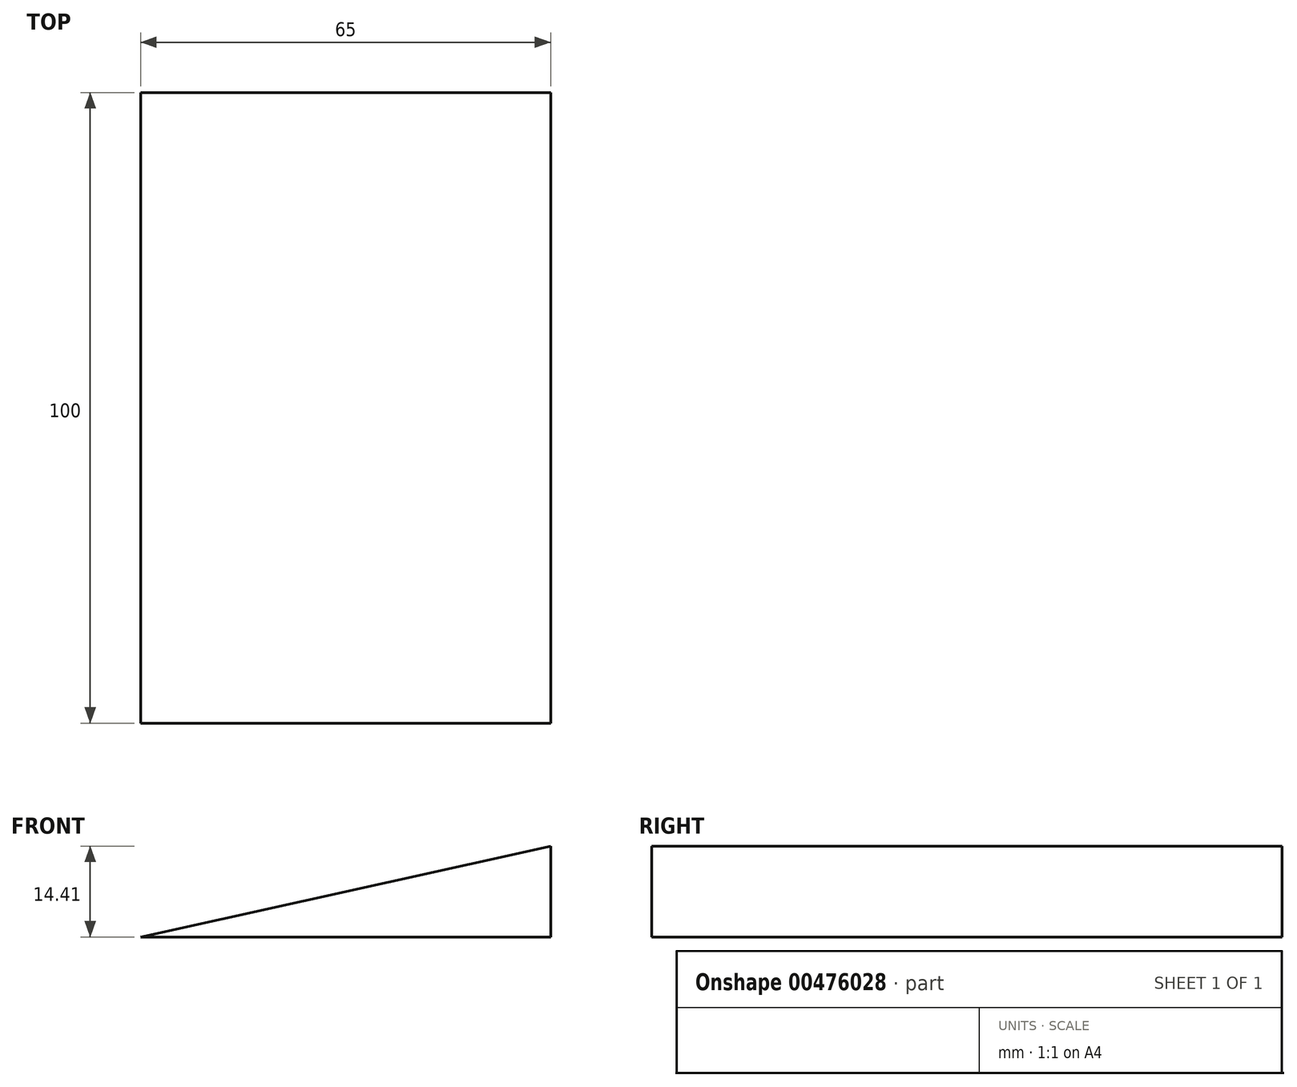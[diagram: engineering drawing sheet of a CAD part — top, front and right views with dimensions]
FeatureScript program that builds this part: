
annotation { "Feature Type Name" : "Feature", "Feature Type Description" : "" }
export const myFeature = defineFeature(function(context is Context, id is Id, definition is map)
    precondition{}
    {
        {
            var Q0;
            Q0=qCreatedBy(makeId("Front.planeOp"),FACE);
            var sketch = newSketch(context, id + "F0", { "sketchPlane" : qUnion([Q0])});
            skLineSegment(sketch, "E0", {"start": v(0, 0) * mm, "end": v(0, 14.41) * mm});
            skLineSegment(sketch, "E1", {"start": v(0, 14.41) * mm, "end": v(-65, 0) * mm});
            skLineSegment(sketch, "E2", {"start": v(-65, 0) * mm, "end": v(0, 0) * mm});
            skSolve(sketch);
        }
        {
            var Q0;
            Q0 = qSketchRegion(id + "F0", true);
            extrude(context, id + "F1", {"entities" : qUnion([Q0]), "depth" : 100 * mm});
        }
    });
